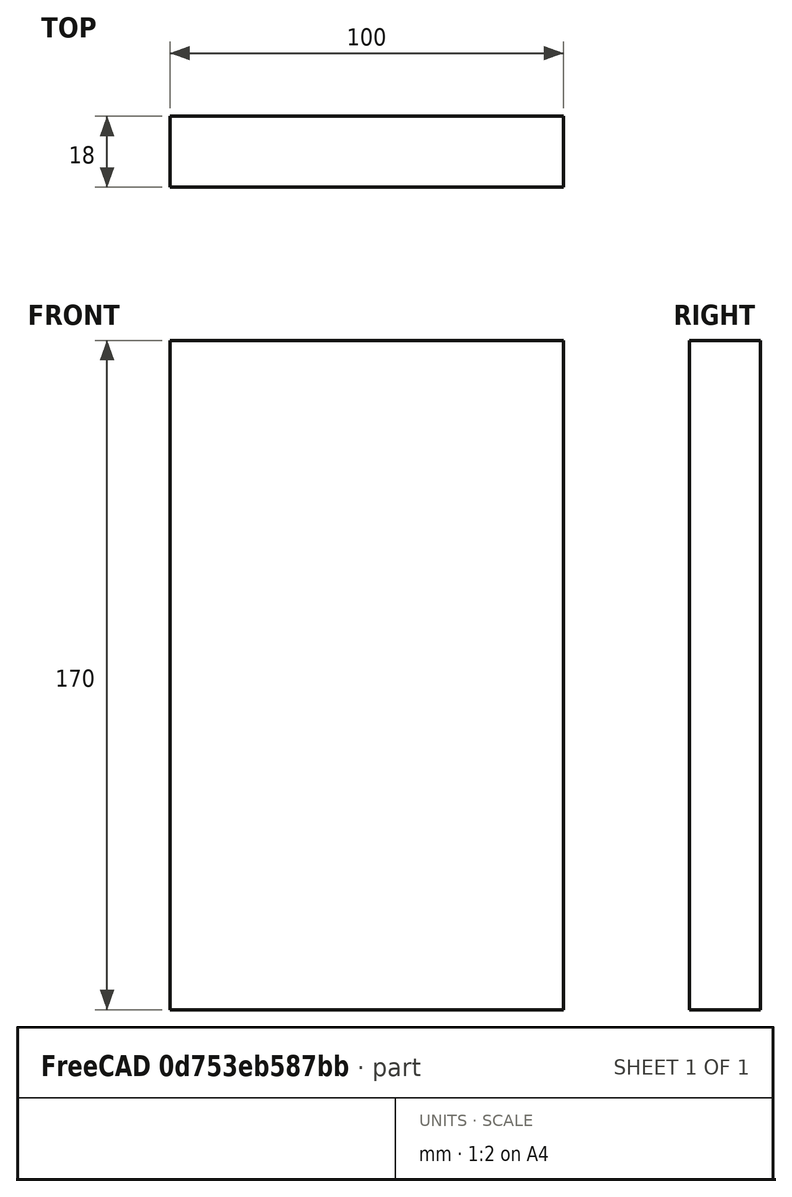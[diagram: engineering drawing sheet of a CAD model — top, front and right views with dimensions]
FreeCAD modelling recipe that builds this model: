
FCSTD DOCUMENT  (FreeCAD 0.18R4 (GitTag))
Label: back
License: All rights reserved
LicenseURL: http://en.wikipedia.org/wiki/All_rights_reserved
objects: Sketcher::SketchObject×1, PartDesign::Pad×1, PartDesign::Body×1
note: 4 computed .brp shape members not serialized (recipe doc carries the construction recipe); baked Part::Feature solids carry a one-line shape summary decoded from their .brp

FEATURE [Sketcher::SketchObject] Sketch
  MapMode = 5
  Placement = pos=(0,0,0) rot=(1,0,0;1.5708rad)
  Support = -> [XZ_Plane]
  sketch-geometry (4):
    g0: LineSegment StartX=0 StartY=0 StartZ=0 EndX=-100 EndY=0 EndZ=0
    g1: LineSegment StartX=-100 StartY=0 StartZ=0 EndX=-100 EndY=170 EndZ=0
    g2: LineSegment StartX=-100 StartY=170 StartZ=0 EndX=0 EndY=170 EndZ=0
    g3: LineSegment StartX=0 StartY=170 StartZ=0 EndX=0 EndY=0 EndZ=0
  constraints (11):
    c: Coincident(g0,g1)
    c: Coincident(g1,g2)
    c: Coincident(g2,g3)
    c: Coincident(g3,g0)
    c: Horizontal(g0)
    c: Horizontal(g2)
    c: Vertical(g1)
    c: Vertical(g3)
    c: Coincident(g0,g-1)
    c: DistanceY(g3,g3) = 170
    c: DistanceX(g0,g0) = 100
FEATURE [PartDesign::Pad] Pad
  Length = 18
  Length2 = 100
  Placement = pos=(0,0,0) rot=(1,0,0;1.5708rad)
  Profile = -> Sketch
  Type = 0
FEATURE [PartDesign::Body] Body
  Group = -> [Sketch,Pad]
  Origin = -> Origin
  Tip = -> Pad
